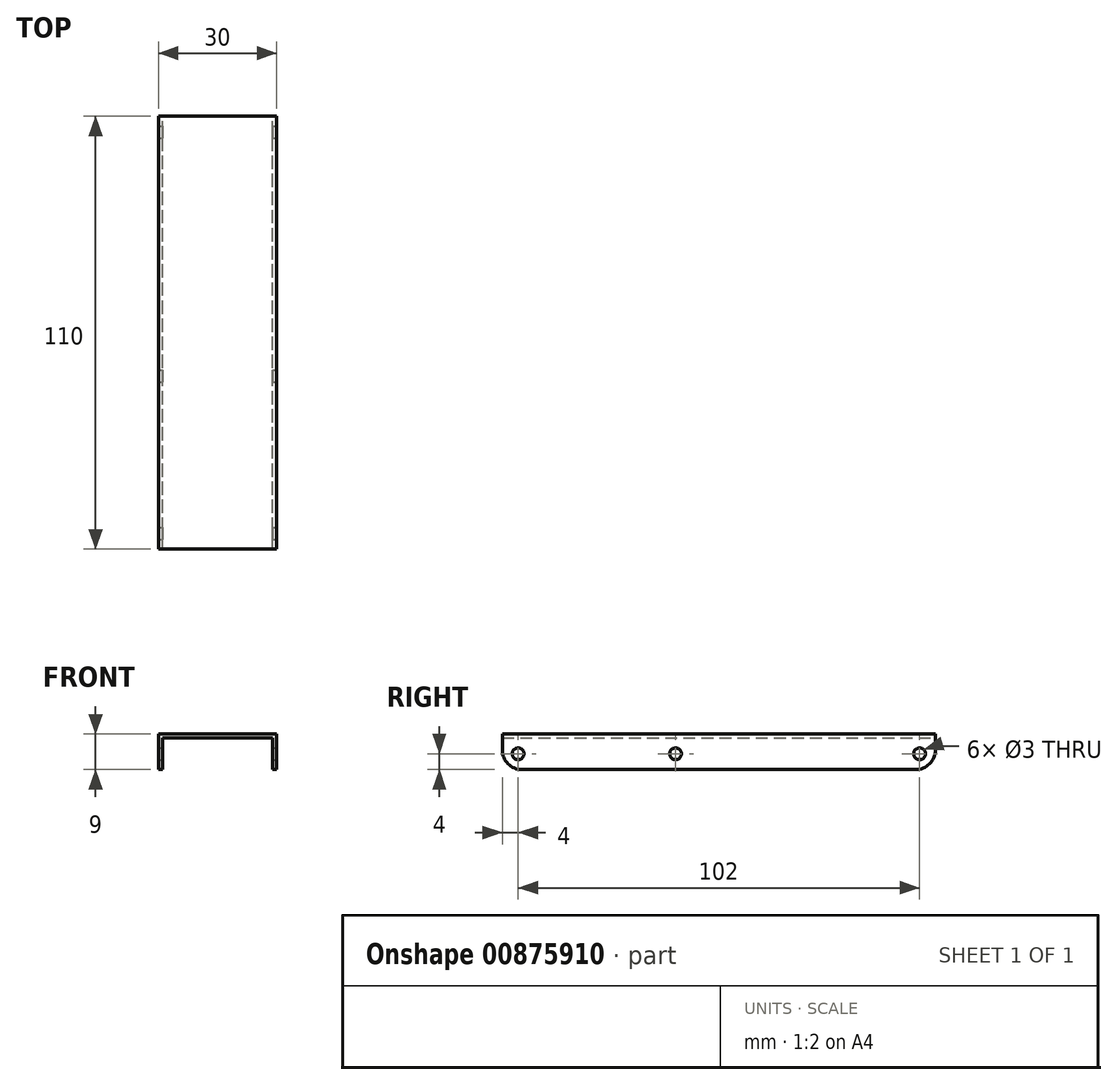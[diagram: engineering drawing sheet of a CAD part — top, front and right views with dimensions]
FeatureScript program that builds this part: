
annotation { "Feature Type Name" : "Feature", "Feature Type Description" : "" }
export const myFeature = defineFeature(function(context is Context, id is Id, definition is map)
    precondition{}
    {
        {
            var Q0;
            Q0=qCreatedBy(makeId("Front.planeOp"),FACE);
            var sketch = newSketch(context, id + "F0", { "sketchPlane" : qUnion([Q0])});
            skLineSegment(sketch, "E0.bottom", {"start": v(-15, 0) * mm, "end": v(15, 0) * mm});
            skLineSegment(sketch, "E0.top", {"start": v(-15, -9) * mm, "end": v(-14, -9) * mm});
            skLineSegment(sketch, "E0.left", {"start": v(-15, 0) * mm, "end": v(-15, -9) * mm});
            skLineSegment(sketch, "E0.right", {"start": v(15, 0) * mm, "end": v(15, -9) * mm});
            skLineSegment(sketch, "E1.bottom", {"start": v(-14, -1) * mm, "end": v(14, -1) * mm});
            skLineSegment(sketch, "E1.left", {"start": v(-14, -1) * mm, "end": v(-14, -9) * mm});
            skLineSegment(sketch, "E1.right", {"start": v(14, -1) * mm, "end": v(14, -9) * mm});
            skLineSegment(sketch, "E2.trimOffspring", {"start": v(14, -9) * mm, "end": v(15, -9) * mm});
            skSolve(sketch);
        }
        {
            var Q0;
            Q0 = qSketchRegion(id + "F0", true);
            extrude(context, id + "F1", {"entities" : qUnion([Q0]), "depth" : 110 * mm, "offsetDistance" : 25 * mm});
        }
        {
            var Q0;
            Q0=makeQuery(id+"F1.opExtrude","SWEPT_FACE",FACE,{"disambiguationData":[OSD([sQuery(id+"F0.wireOp",EDGE,"E0.right")])]});
            var sketch = newSketch(context, id + "F2", { "sketchPlane" : qUnion([Q0])});
            skCircle(sketch, "E3", {"center": v(-106, -5) * mm, "radius": 1.5 * mm});
            skCircle(sketch, "E4", {"center": v(-66, -5) * mm, "radius": 1.5 * mm});
            skCircle(sketch, "E5", {"center": v(-4, -5) * mm, "radius": 1.5 * mm});
            skSolve(sketch);
        }
        {
            var Q0;
            Q0 = qSketchRegion(id + "F2", true);
            extrude(context, id + "F3", {"entities" : qUnion([Q0]), "operationType" : NewBodyOperationType.REMOVE, "oppositeDirection" : true, "depth" : 35 * mm, "offsetDistance" : 25 * mm});
        }
        {
            var Q0;
            Q0=makeQuery(id+"F1.opExtrude","CAP_EDGE",EDGE,{"disambiguationData":[OSD([sQuery(id+"F0.wireOp",EDGE,"E2.trimOffspring")])],"isStart":false});
            var Q1;
            Q1=makeQuery(id+"F1.opExtrude","CAP_EDGE",EDGE,{"disambiguationData":[OSD([sQuery(id+"F0.wireOp",EDGE,"E0.top")])],"isStart":false});
            var Q2;
            Q2=makeQuery(id+"F1.opExtrude","CAP_EDGE",EDGE,{"disambiguationData":[OSD([sQuery(id+"F0.wireOp",EDGE,"E2.trimOffspring")])],"isStart":true});
            var Q3;
            Q3=makeQuery(id+"F1.opExtrude","CAP_EDGE",EDGE,{"disambiguationData":[OSD([sQuery(id+"F0.wireOp",EDGE,"E0.top")])],"isStart":true});
            fillet(context, id + "F4", {"entities" : qUnion([Q0, Q1, Q2, Q3]), "radius" : 5 * mm, "tangentPropagation" : true, "allowEdgeOverflow" : false});
        }
    });
